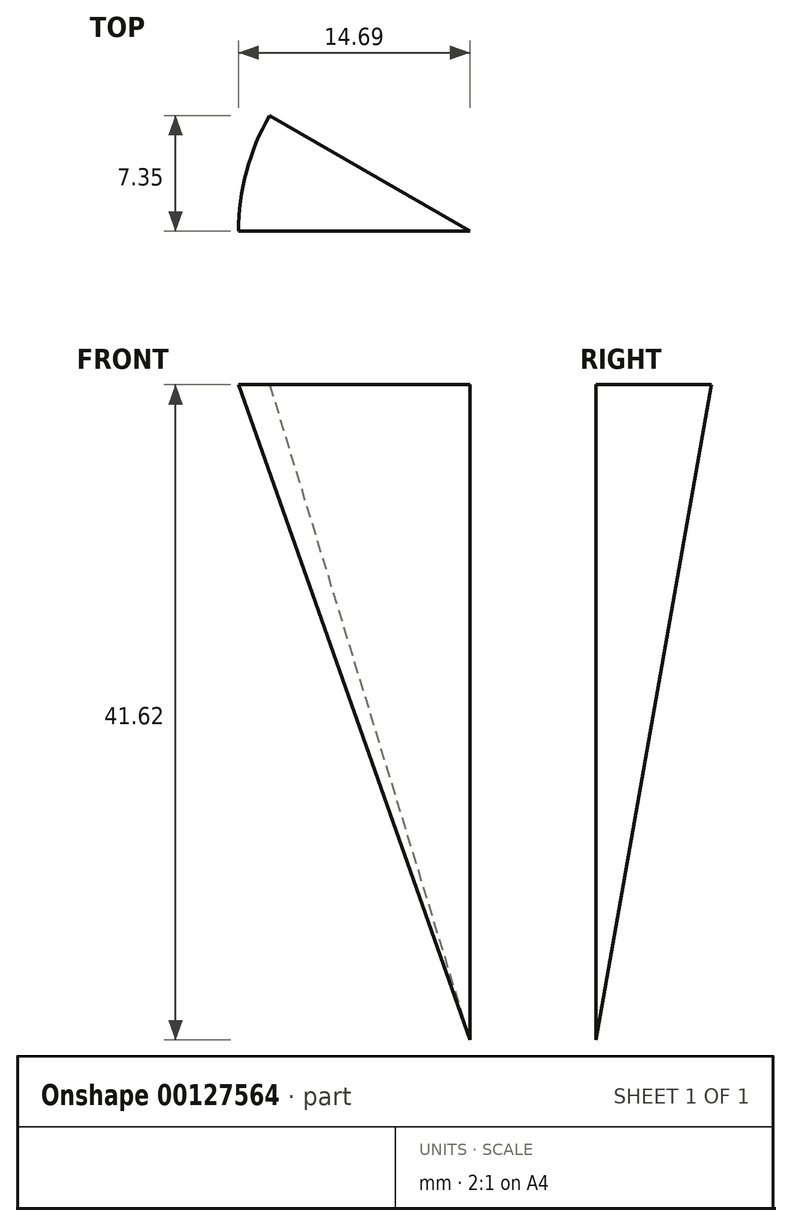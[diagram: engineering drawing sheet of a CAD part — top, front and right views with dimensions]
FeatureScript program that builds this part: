
annotation { "Feature Type Name" : "Feature", "Feature Type Description" : "" }
export const myFeature = defineFeature(function(context is Context, id is Id, definition is map)
    precondition{}
    {
        {
            var Q0;
            Q0=qCreatedBy(makeId("Front.planeOp"),FACE);
            var sketch = newSketch(context, id + "F0", { "sketchPlane" : qUnion([Q0])});
            skLineSegment(sketch, "E0", {"start": v(0, 41.62) * mm, "end": v(0, -85.38) * mm});
            skLineSegment(sketch, "E1", {"start": v(0, 41.62) * mm, "end": v(-76.2, 41.62) * mm});
            skLineSegment(sketch, "E2", {"start": v(-76.2, 41.62) * mm, "end": v(-76.2, -85.38) * mm});
            skLineSegment(sketch, "E3", {"start": v(-76.2, -85.38) * mm, "end": v(0, -85.38) * mm});
            skLineSegment(sketch, "E4", {"start": v(-14.7, 41.62) * mm, "end": v(0, 0) * mm});
            skLineSegment(sketch, "E5", {"start": v(-66.58, 41.62) * mm, "end": v(-46.95, 0) * mm});
            skLineSegment(sketch, "E6", {"start": v(-32.85, 41.62) * mm, "end": v(-46.95, 0) * mm});
            skLineSegment(sketch, "E7", {"start": v(-66.58, 41.62) * mm, "end": v(-32.85, 41.62) * mm});
            skLineSegment(sketch, "E8", {"start": v(-14.7, 41.62) * mm, "end": v(0, 41.62) * mm});
            skLineSegment(sketch, "E9", {"start": v(0, 41.62) * mm, "end": v(0, 0) * mm});
            skLineSegment(sketch, "E10", {"start": v(-32.85, 41.62) * mm, "end": v(-14.7, 41.62) * mm});
            skSolve(sketch);
        }
        {
            var Q0;
            Q0=makeQuery(id+"F0.imprint","IMPRINT",FACE,{"disambiguationData":[TD([[makeQuery(id+"F0.imprint","IMPRINT",EDGE,{"derivedFrom":sQuery(id+"F0.wireOp",EDGE,"E0")}),-1.0]])]});
            var Q1;
            Q1=sQuery(id+"F0.wireOp",EDGE,"E0");
            revolve(context, id + "F1", {"entities" : qUnion([Q0]), "axis" : qUnion([Q1]), "revolveType" : RevolveType.ONE_DIRECTION, "angle" : 30 * degree});
        }
    });
